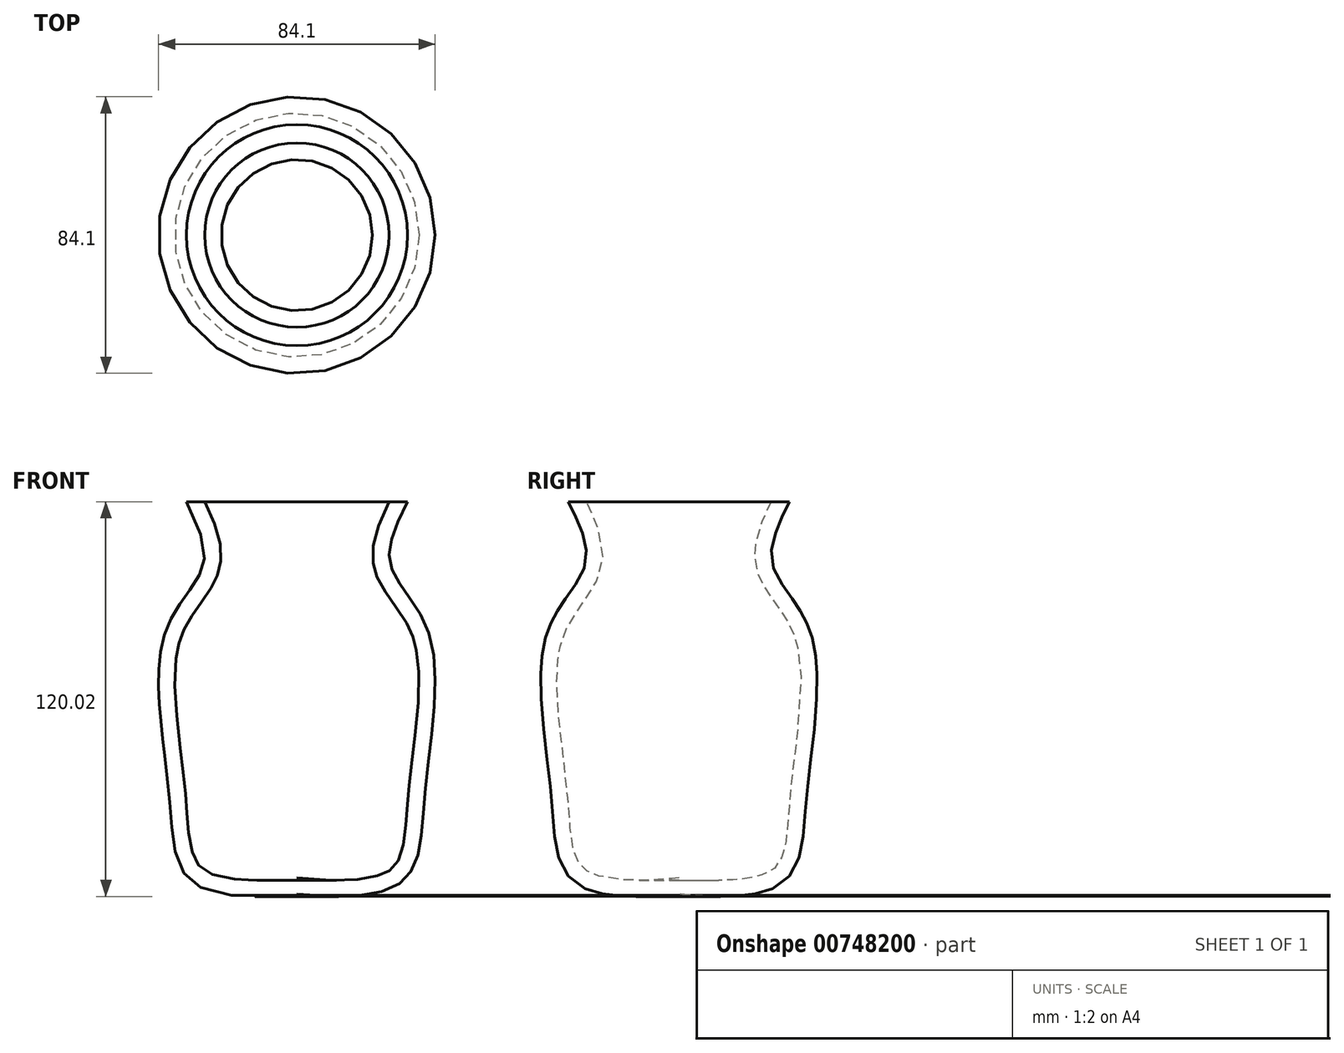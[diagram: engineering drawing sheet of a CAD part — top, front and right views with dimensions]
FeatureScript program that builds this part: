
annotation { "Feature Type Name" : "Feature", "Feature Type Description" : "" }
export const myFeature = defineFeature(function(context is Context, id is Id, definition is map)
    precondition{}
    {
        {
            var Q0;
            Q0=qCreatedBy(makeId("Front.planeOp"),FACE);
            var sketch = newSketch(context, id + "F0", { "sketchPlane" : qUnion([Q0])});
            skFitSpline(sketch, "E0", {"points": [v(38.23, 64.5) * mm, v(28.33, 36.07) * mm, v(40.1, 15.05) * mm, v(38.83, -34.5) * mm, v(31.03, -61.26) * mm, v(-43.57, -56.64) * mm], "startDerivative": vector(-103.95, -225.43) * mm, "endDerivative": vector(-340.6, 74.37) * mm});
            skLineSegment(sketch, "E1", {"start": v(0, 23.75) * mm, "end": v(0, -70.4) * mm});
            skLineSegment(sketch, "E2", {"start": v(21.08, 54.95) * mm, "end": v(45.25, 54.95) * mm});
            skFitSpline(sketch, "E3.0", {"points": [v(33.69, 66.6) * mm, v(32.63, 64.31) * mm, v(30.54, 60.01) * mm, v(27.66, 54.23) * mm, v(25.63, 49.77) * mm, v(24.35, 46.3) * mm, v(23.6, 43.67) * mm, v(23.1, 41) * mm, v(23, 38.72) * mm, v(23.12, 36.87) * mm, v(23.33, 35.48) * mm, v(23.66, 34.1) * mm, v(24.1, 32.8) * mm, v(24.61, 31.55) * mm, v(25.38, 29.98) * mm, v(26.46, 28.14) * mm, v(27.85, 26.07) * mm, v(29.27, 24.07) * mm, v(30.68, 22.1) * mm, v(32.02, 20.14) * mm, v(33.25, 18.14) * mm, v(34.15, 16.43) * mm, v(34.78, 15.02) * mm, v(35.2, 13.93) * mm, v(35.57, 12.82) * mm, v(35.9, 11.63) * mm, v(36.19, 10.38) * mm, v(36.51, 8.63) * mm, v(36.93, 5.34) * mm, v(37.13, 0.14) * mm, v(36.84, -6.7) * mm, v(36.17, -13.88) * mm, v(35.45, -19.98) * mm, v(34.85, -24.84) * mm, v(34.43, -28.46) * mm, v(34.1, -31.43) * mm, v(33.87, -33.76) * mm, v(33.67, -36.07) * mm, v(33.46, -38.83) * mm, v(33.23, -41.93) * mm, v(32.98, -44.8) * mm, v(32.67, -47.43) * mm, v(32.28, -49.77) * mm, v(31.78, -51.8) * mm, v(31.17, -53.48) * mm, v(30.47, -54.84) * mm, v(29.66, -55.93) * mm, v(28.86, -56.69) * mm, v(28.07, -57.24) * mm, v(27.37, -57.65) * mm, v(26.55, -58.04) * mm, v(25.3, -58.54) * mm, v(23.45, -59.08) * mm, v(20.8, -59.59) * mm, v(17.74, -59.92) * mm, v(13.21, -60.14) * mm, v(6.77, -59.98) * mm, v(-1.95, -59.17) * mm, v(-11.43, -57.84) * mm, v(-21.48, -56.1) * mm, v(-31.9, -54.03) * mm, v(-38.97, -52.52) * mm, v(-42.5, -51.75) * mm]});
            skSolve(sketch);
        }
        {
            var Q0;
            {var subQ0=sQuery(id+"F0.wireOp",EDGE,"E1");var subQ1=sQuery(id+"F0.wireOp",EDGE,"E0");var subQ2=makeQuery(id+"F0.imprint","INTERSECT",VERTEX,{"derivedFrom":[subQ1,subQ0]});Q0=makeQuery(id+"F0.imprint","IMPRINT",FACE,{"disambiguationData":[TD([[makeQuery(id+"F0.imprint","IMPRINT",EDGE,{"disambiguationData":[TD([[subQ2,1.0]])],"derivedFrom":subQ1}),-1.0]])]});}
            var Q1;
            Q1=sQuery(id+"F0.wireOp",EDGE,"E1");
            revolve(context, id + "F1", {"surfaceOperationType" : NewSurfaceOperationType.NEW, "entities" : qUnion([Q0]), "axis" : qUnion([Q1]), "revolveType" : RevolveType.FULL});
        }
    });
